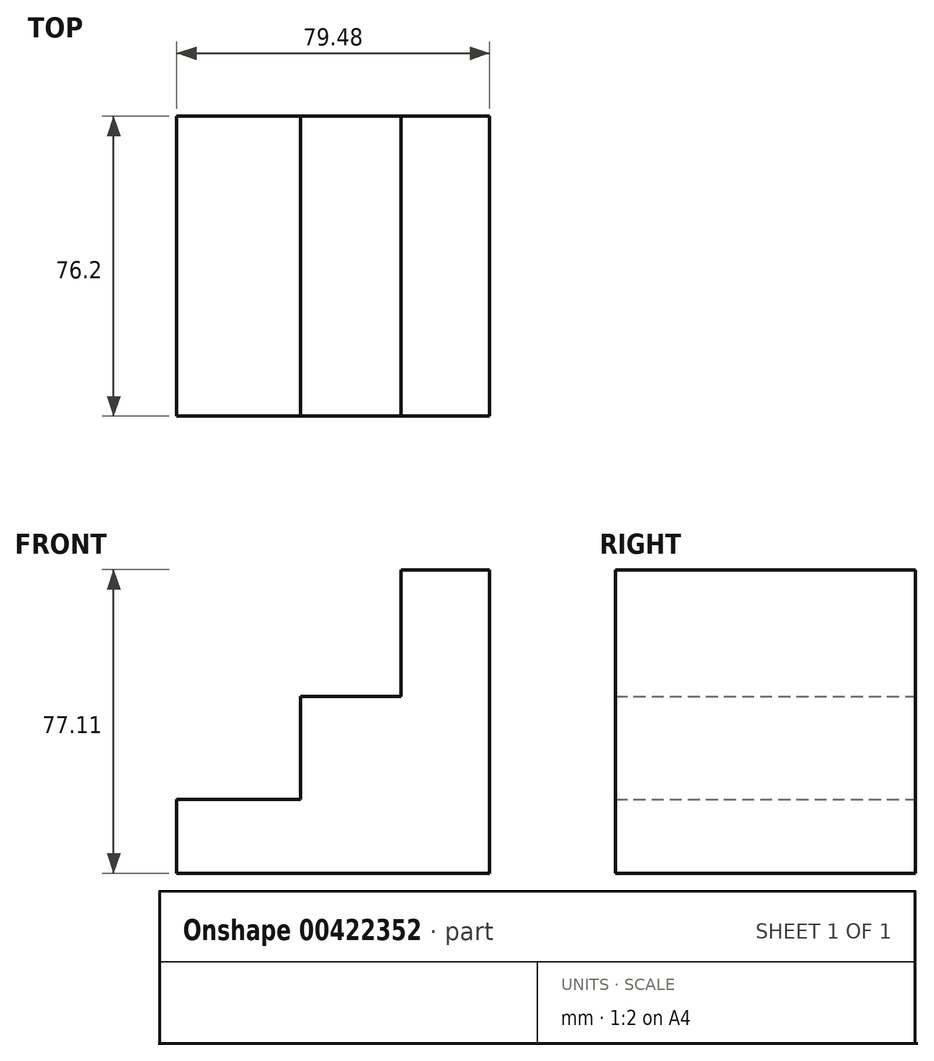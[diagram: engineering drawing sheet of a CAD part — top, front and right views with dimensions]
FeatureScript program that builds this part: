
annotation { "Feature Type Name" : "Feature", "Feature Type Description" : "" }
export const myFeature = defineFeature(function(context is Context, id is Id, definition is map)
    precondition{}
    {
        {
            var Q0;
            Q0=qCreatedBy(makeId("Front.planeOp"),FACE);
            var sketch = newSketch(context, id + "F0", { "sketchPlane" : qUnion([Q0])});
            skLineSegment(sketch, "E0", {"start": v(-35.12, -29.84) * mm, "end": v(42.78, -29.84) * mm});
            skLineSegment(sketch, "E1", {"start": v(42.78, -29.84) * mm, "end": v(42.78, 47.27) * mm});
            skLineSegment(sketch, "E2", {"start": v(42.78, 47.27) * mm, "end": v(20.33, 47.27) * mm});
            skLineSegment(sketch, "E3", {"start": v(20.33, 47.27) * mm, "end": v(20.33, 15.05) * mm});
            skLineSegment(sketch, "E4", {"start": v(20.33, 15.05) * mm, "end": v(-5.28, 15.05) * mm});
            skLineSegment(sketch, "E5", {"start": v(-5.28, 15.05) * mm, "end": v(-5.28, -11.1) * mm});
            skLineSegment(sketch, "E6", {"start": v(-5.28, -11.1) * mm, "end": v(-36.7, -11.1) * mm});
            skLineSegment(sketch, "E7", {"start": v(-36.7, -11.1) * mm, "end": v(-36.7, -29.84) * mm});
            skLineSegment(sketch, "E8", {"start": v(-36.7, -29.84) * mm, "end": v(-35.12, -29.84) * mm});
            skSolve(sketch);
        }
        {
            var Q0;
            Q0 = qSketchRegion(id + "F0", true);
            extrude(context, id + "F1", {"entities" : qUnion([Q0]), "depth" : 76.2 * mm});
        }
    });
